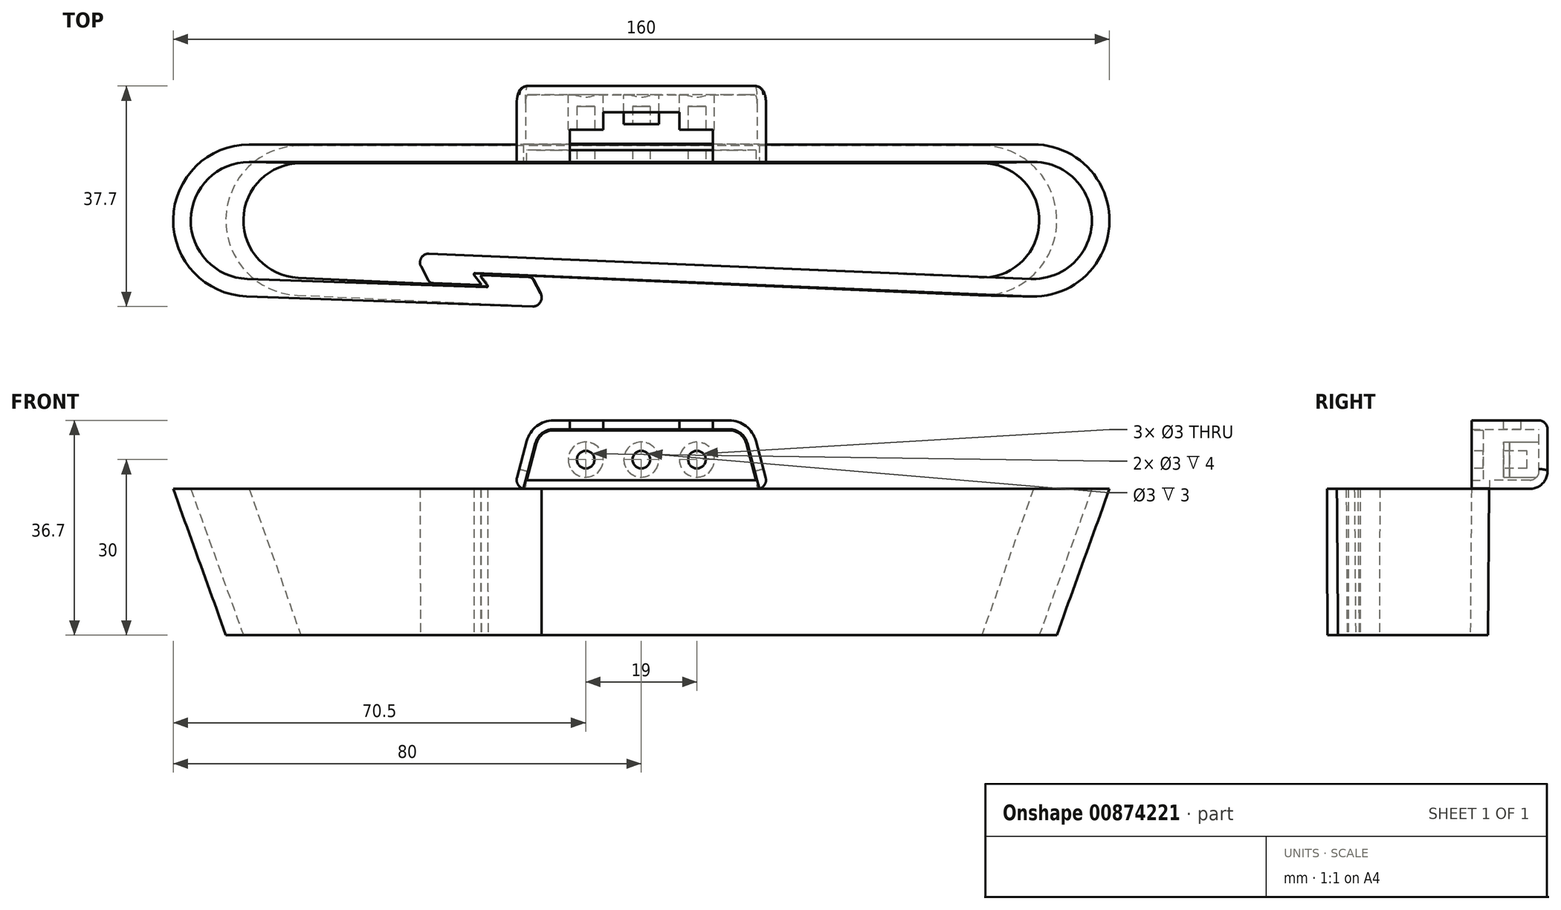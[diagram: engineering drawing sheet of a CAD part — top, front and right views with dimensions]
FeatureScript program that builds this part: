
annotation { "Feature Type Name" : "Feature", "Feature Type Description" : "" }
export const myFeature = defineFeature(function(context is Context, id is Id, definition is map)
    precondition{}
    {
        {
            var Q0;
            Q0=qCreatedBy(makeId("Top.planeOp"),FACE);
            var sketch = newSketch(context, id + "F0", { "sketchPlane" : qUnion([Q0])});
            skPoint(sketch, "E0.middle", {"position": v(0, 0) * mm});
            skArc(sketch, "E1", {"start": v(66.46, -12.99) * mm, "mid": v(80, -0.27) * mm, "end": v(67, 13) * mm});
            skLineSegment(sketch, "E2", {"start": v(67, 13) * mm, "end": v(-67, 13) * mm});
            skArc(sketch, "E3", {"start": v(-67, 13) * mm, "mid": v(-80, 0.23) * mm, "end": v(-67.45, -13) * mm});
            skLineSegment(sketch, "E4", {"start": v(66.46, -12.99) * mm, "end": v(-28.42, -9.01) * mm});
            skLineSegment(sketch, "E5", {"start": v(0, 13) * mm, "end": v(0, -10.2) * mm, "construction": true});
            skLineSegment(sketch, "E6", {"start": v(-16, 0) * mm, "end": v(-16, -14.79) * mm, "construction": true});
            skLineSegment(sketch, "E7", {"start": v(-67.45, -13) * mm, "end": v(-18.6, -14.7) * mm});
            skLineSegment(sketch, "E8", {"start": v(-67, 0) * mm, "end": v(-16, 0) * mm, "construction": true});
            skLineSegment(sketch, "E9.0", {"start": v(66.58, -10) * mm, "end": v(-36.26, -5.68) * mm});
            skLineSegment(sketch, "E9.1", {"start": v(-67.35, -10) * mm, "end": v(-26.46, -11.42) * mm});
            skArc(sketch, "E9.2", {"start": v(-67, 10) * mm, "mid": v(-77, 0.17) * mm, "end": v(-67.35, -10) * mm});
            skLineSegment(sketch, "E9.3", {"start": v(67, 10) * mm, "end": v(-67, 10) * mm});
            skArc(sketch, "E9.4", {"start": v(66.58, -10) * mm, "mid": v(77, -0.2) * mm, "end": v(67, 10) * mm});
            skLineSegment(sketch, "E10", {"start": v(-27.2, -9.4) * mm, "end": v(-19.29, -9.67) * mm});
            skLineSegment(sketch, "E11", {"start": v(-18.44, -10.2) * mm, "end": v(-17.22, -12.5) * mm});
            skPoint(sketch, "E12.visualSharp", {"position": v(-16, -14.79) * mm});
            skArc(sketch, "E12.filletArc", {"start": v(-18.6, -14.7) * mm, "mid": v(-17.27, -14) * mm, "end": v(-17.22, -12.5) * mm});
            skPoint(sketch, "E13.visualSharp", {"position": v(-18.71, -9.7) * mm});
            skArc(sketch, "E13.filletArc", {"start": v(-18.44, -10.2) * mm, "mid": v(-18.8, -9.82) * mm, "end": v(-19.29, -9.67) * mm});
            skPoint(sketch, "E14.visualSharp", {"position": v(-27.2, -9.4) * mm});
            skArc(sketch, "E14.filletArc", {"start": v(-27.2, -9.4) * mm, "mid": v(-27.4, -9.5) * mm, "end": v(-27.37, -9.72) * mm});
            skLineSegment(sketch, "E15", {"start": v(0, 0) * mm, "end": v(67, 0) * mm, "construction": true});
            skLineSegment(sketch, "E16", {"start": v(-28.59, -9.33) * mm, "end": v(-27.52, -10.72) * mm});
            skLineSegment(sketch, "E17", {"start": v(-27.69, -11.04) * mm, "end": v(-35.6, -10.71) * mm});
            skLineSegment(sketch, "E18", {"start": v(-36.45, -10.18) * mm, "end": v(-37.65, -7.87) * mm});
            skPoint(sketch, "E19.visualSharp", {"position": v(-36.18, -10.69) * mm});
            skArc(sketch, "E19.filletArc", {"start": v(-36.45, -10.18) * mm, "mid": v(-36.1, -10.56) * mm, "end": v(-35.6, -10.71) * mm});
            skPoint(sketch, "E20.visualSharp", {"position": v(-38.85, -5.57) * mm});
            skArc(sketch, "E20.filletArc", {"start": v(-36.26, -5.68) * mm, "mid": v(-37.59, -6.38) * mm, "end": v(-37.65, -7.87) * mm});
            skArc(sketch, "E21.filletArc", {"start": v(-27.69, -11.04) * mm, "mid": v(-27.5, -10.94) * mm, "end": v(-27.52, -10.72) * mm});
            skPoint(sketch, "E22.visualSharp", {"position": v(-28.85, -9) * mm});
            skArc(sketch, "E22.filletArc", {"start": v(-28.42, -9.01) * mm, "mid": v(-28.6, -9.12) * mm, "end": v(-28.59, -9.33) * mm});
            skLineSegment(sketch, "E23", {"start": v(-16, 0) * mm, "end": v(0, 0) * mm, "construction": true});
            skArc(sketch, "E24", {"start": v(-26.46, -11.42) * mm, "mid": v(-26.27, -11.31) * mm, "end": v(-26.3, -11.1) * mm});
            skLineSegment(sketch, "E25", {"start": v(-27.37, -9.72) * mm, "end": v(-26.3, -11.1) * mm});
            skLineSegment(sketch, "E26", {"start": v(-27.37, -9.47) * mm, "end": v(-27.37, -10.97) * mm, "construction": true});
            skLineSegment(sketch, "E27", {"start": v(-27.52, -10.72) * mm, "end": v(-27.52, -9.22) * mm, "construction": true});
            skSolve(sketch);
        }
        {
            var Q0;
            Q0=qCreatedBy(makeId("Top.planeOp"),FACE);
            cPlane(context, id + "F1", {"entities" : qUnion([Q0]), "cplaneType" : CPlaneType.OFFSET, "offset" : 25 * mm, "oppositeDirection" : true, "width" : 150 * mm, "height" : 150 * mm});
        }
        {
            var Q0;
            Q0=qCreatedBy(id+"F1.planeOp",FACE);
            var sketch = newSketch(context, id + "F2", { "sketchPlane" : qUnion([Q0])});
            skPoint(sketch, "E28.middle", {"position": v(0, 0) * mm});
            skArc(sketch, "E29", {"start": v(57.64, -12.79) * mm, "mid": v(71, -0.28) * mm, "end": v(58.2, 12.8) * mm});
            skLineSegment(sketch, "E30", {"start": v(58.2, 12.8) * mm, "end": v(-58.2, 12.8) * mm});
            skArc(sketch, "E31", {"start": v(-58.2, 12.8) * mm, "mid": v(-71, 0.3) * mm, "end": v(-58.78, -12.79) * mm});
            skLineSegment(sketch, "E32", {"start": v(57.64, -12.79) * mm, "end": v(-28.37, -9.03) * mm});
            skLineSegment(sketch, "E33", {"start": v(0, 12.8) * mm, "end": v(0, -10.27) * mm, "construction": true});
            skLineSegment(sketch, "E34", {"start": v(-16, 0) * mm, "end": v(-16, -14.73) * mm, "construction": true});
            skLineSegment(sketch, "E35", {"start": v(-58.78, -12.79) * mm, "end": v(-18.6, -14.61) * mm});
            skLineSegment(sketch, "E36", {"start": v(-58.2, 0) * mm, "end": v(-16, 0) * mm, "construction": true});
            skLineSegment(sketch, "E37.0", {"start": v(57.77, -9.8) * mm, "end": v(-36.2, -5.69) * mm});
            skLineSegment(sketch, "E37.1", {"start": v(-58.64, -9.79) * mm, "end": v(-26.42, -11.25) * mm});
            skArc(sketch, "E37.2", {"start": v(-58.2, 9.8) * mm, "mid": v(-68, 0.22) * mm, "end": v(-58.64, -9.79) * mm});
            skLineSegment(sketch, "E37.3", {"start": v(58.2, 9.8) * mm, "end": v(-58.2, 9.8) * mm});
            skArc(sketch, "E37.4", {"start": v(57.77, -9.8) * mm, "mid": v(68, -0.21) * mm, "end": v(58.2, 9.8) * mm});
            skLineSegment(sketch, "E38", {"start": v(-27.15, -9.22) * mm, "end": v(-19.23, -9.58) * mm});
            skLineSegment(sketch, "E39", {"start": v(-18.4, -10.12) * mm, "end": v(-17.2, -12.42) * mm});
            skPoint(sketch, "E40.visualSharp", {"position": v(-16, -14.73) * mm});
            skArc(sketch, "E40.filletArc", {"start": v(-18.6, -14.61) * mm, "mid": v(-17.26, -13.92) * mm, "end": v(-17.2, -12.42) * mm});
            skPoint(sketch, "E41.visualSharp", {"position": v(-18.66, -9.6) * mm});
            skArc(sketch, "E41.filletArc", {"start": v(-18.4, -10.12) * mm, "mid": v(-18.74, -9.73) * mm, "end": v(-19.23, -9.58) * mm});
            skPoint(sketch, "E42.visualSharp", {"position": v(-27.15, -9.22) * mm});
            skArc(sketch, "E42.filletArc", {"start": v(-27.15, -9.22) * mm, "mid": v(-27.33, -9.33) * mm, "end": v(-27.32, -9.54) * mm});
            skLineSegment(sketch, "E43", {"start": v(0, 0) * mm, "end": v(58.2, 0) * mm, "construction": true});
            skLineSegment(sketch, "E44", {"start": v(-28.53, -9.35) * mm, "end": v(-27.47, -10.74) * mm});
            skLineSegment(sketch, "E45", {"start": v(-27.63, -11.07) * mm, "end": v(-35.55, -10.72) * mm});
            skLineSegment(sketch, "E46", {"start": v(-36.4, -10.18) * mm, "end": v(-37.6, -7.88) * mm});
            skPoint(sketch, "E47.visualSharp", {"position": v(-36.13, -10.7) * mm});
            skArc(sketch, "E47.filletArc", {"start": v(-36.4, -10.18) * mm, "mid": v(-36.04, -10.57) * mm, "end": v(-35.55, -10.72) * mm});
            skPoint(sketch, "E48.visualSharp", {"position": v(-38.8, -5.57) * mm});
            skArc(sketch, "E48.filletArc", {"start": v(-36.2, -5.69) * mm, "mid": v(-37.53, -6.38) * mm, "end": v(-37.6, -7.88) * mm});
            skArc(sketch, "E49.filletArc", {"start": v(-27.63, -11.07) * mm, "mid": v(-27.45, -10.96) * mm, "end": v(-27.47, -10.74) * mm});
            skPoint(sketch, "E50.visualSharp", {"position": v(-28.8, -9.01) * mm});
            skArc(sketch, "E50.filletArc", {"start": v(-28.37, -9.03) * mm, "mid": v(-28.55, -9.14) * mm, "end": v(-28.53, -9.35) * mm});
            skLineSegment(sketch, "E51", {"start": v(-16, 0) * mm, "end": v(0, 0) * mm, "construction": true});
            skArc(sketch, "E52", {"start": v(-26.42, -11.25) * mm, "mid": v(-26.23, -11.15) * mm, "end": v(-26.25, -10.93) * mm});
            skLineSegment(sketch, "E53", {"start": v(-27.32, -9.54) * mm, "end": v(-26.25, -10.93) * mm});
            skLineSegment(sketch, "E54", {"start": v(-27.32, -9.3) * mm, "end": v(-27.32, -10.8) * mm, "construction": true});
            skLineSegment(sketch, "E55", {"start": v(-27.47, -10.74) * mm, "end": v(-27.47, -9.24) * mm, "construction": true});
            skSolve(sketch);
        }
        {
            var Q0;
            Q0=qSketchRegion(id+"F0",true);
            var Q1;
            Q1=qSketchRegion(id+"F2",true);
            loft(context, id + "F3", {"sheetProfilesArray" : [{ "sheetProfileEntities" : qUnion([Q0]) }, { "sheetProfileEntities" : qUnion([Q1]) }]});
        }
        {
            var Q0;
            Q0=qCreatedBy(makeId("Top.planeOp"),FACE);
            var sketch = newSketch(context, id + "F4", { "sketchPlane" : qUnion([Q0])});
            skLineSegment(sketch, "E56", {"start": v(20, 12) * mm, "end": v(20, 10) * mm});
            skLineSegment(sketch, "E57", {"start": v(20, 10) * mm, "end": v(-20, 10) * mm});
            skLineSegment(sketch, "E58", {"start": v(-20, 10) * mm, "end": v(-20, 12) * mm});
            skLineSegment(sketch, "E59", {"start": v(-20, 12) * mm, "end": v(20, 12) * mm});
            skPoint(sketch, "E60.visualSharp", {"position": v(-20, 10) * mm});
            skPoint(sketch, "E61.visualSharp", {"position": v(20, 10) * mm});
            skLineSegment(sketch, "E62", {"start": v(0, 10) * mm, "end": v(0, 12) * mm, "construction": true});
            skPoint(sketch, "E62.endSnap0", {"position": v(0, 12) * mm});
            skSolve(sketch);
        }
        {
            var Q0;
            Q0=qSketchRegion(id+"F4",true);
            extrude(context, id + "F5", {"entities" : qUnion([Q0]), "operationType" : NewBodyOperationType.ADD, "depth" : 10 * mm, "offsetDistance" : 25 * mm});
        }
        {
            var Q0;
            Q0=makeQuery(id+"F5.opExtrude","SWEPT_FACE",FACE,{"disambiguationData":[OSD([sQuery(id+"F4.wireOp",EDGE,"E57")])]});
            var sketch = newSketch(context, id + "F6", { "sketchPlane" : qUnion([Q0])});
            skLineSegment(sketch, "E63", {"start": v(0, 10) * mm, "end": v(0, 5) * mm, "construction": true});
            skCircle(sketch, "E64", {"center": v(0, 5) * mm, "radius": 1.5 * mm});
            skCircle(sketch, "E65", {"center": v(9.5, 5) * mm, "radius": 1.5 * mm});
            skCircle(sketch, "E66", {"center": v(-9.5, 5) * mm, "radius": 1.5 * mm});
            skSolve(sketch);
        }
        {
            var Q0;
            Q0=qSketchRegion(id+"F6",true);
            extrude(context, id + "F7", {"entities" : qUnion([Q0]), "operationType" : NewBodyOperationType.REMOVE, "endBound" : BoundingType.THROUGH_ALL, "oppositeDirection" : true, "depth" : 25 * mm, "offsetDistance" : 25 * mm});
        }
        {
            var Q0;
            Q0=makeQuery(id+"F5.opExtrude","CAP_EDGE",EDGE,{"disambiguationData":[OSD([sQuery(id+"F4.wireOp",EDGE,"E58")])],"isStart":false});
            var Q1;
            Q1=makeQuery(id+"F5.opExtrude","CAP_EDGE",EDGE,{"disambiguationData":[OSD([sQuery(id+"F4.wireOp",EDGE,"E56")])],"isStart":false});
            chamfer(context, id + "F8", {"entities" : qUnion([Q0, Q1]), "chamferType" : ChamferType.OFFSET_ANGLE, "width" : 10 * mm, "oppositeDirection" : false, "angle" : 15 * degree, "tangentPropagation" : true});
        }
        {
            var Q0;
            {var subQ0=sQuery(id+"F4.wireOp",EDGE,"E58");Q0=makeQuery(id+"F8.opChamfer","BLEND_EDGE",EDGE,{"blendedFrom":[makeQuery(id+"F5.opExtrude","CAP_EDGE",EDGE,{"disambiguationData":[OSD([subQ0])],"isStart":false}),makeQuery(id+"F5.opExtrude","CAP_FACE",FACE,{"disambiguationData":[OSD([sQuery(id+"F4.wireOp",EDGE,"E56"),sQuery(id+"F4.wireOp",EDGE,"E57"),subQ0,sQuery(id+"F4.wireOp",EDGE,"E59")])],"isStart":false})],"blendedInto":[makeQuery(id+"F5.opExtrude","CAP_FACE",FACE,{"disambiguationData":[OSD([sQuery(id+"F4.wireOp",EDGE,"E56"),sQuery(id+"F4.wireOp",EDGE,"E57"),subQ0,sQuery(id+"F4.wireOp",EDGE,"E59")])],"isStart":false})]});}
            var Q1;
            {var subQ0=sQuery(id+"F4.wireOp",EDGE,"E56");Q1=makeQuery(id+"F8.opChamfer","BLEND_EDGE",EDGE,{"blendedFrom":[makeQuery(id+"F5.opExtrude","CAP_EDGE",EDGE,{"disambiguationData":[OSD([subQ0])],"isStart":false}),makeQuery(id+"F5.opExtrude","CAP_FACE",FACE,{"disambiguationData":[OSD([subQ0,sQuery(id+"F4.wireOp",EDGE,"E57"),sQuery(id+"F4.wireOp",EDGE,"E58"),sQuery(id+"F4.wireOp",EDGE,"E59")])],"isStart":false})],"blendedInto":[makeQuery(id+"F5.opExtrude","CAP_FACE",FACE,{"disambiguationData":[OSD([subQ0,sQuery(id+"F4.wireOp",EDGE,"E57"),sQuery(id+"F4.wireOp",EDGE,"E58"),sQuery(id+"F4.wireOp",EDGE,"E59")])],"isStart":false})]});}
            fillet(context, id + "F9", {"entities" : qUnion([Q0, Q1]), "radius" : 3 * mm, "tangentPropagation" : true, "allowEdgeOverflow" : false});
        }
        {
            var Q0;
            Q0=makeQuery(id+"F5.opExtrude","SWEPT_FACE",FACE,{"disambiguationData":[OSD([sQuery(id+"F4.wireOp",EDGE,"E57")])]});
            cPlane(context, id + "F10", {"entities" : qUnion([Q0]), "cplaneType" : CPlaneType.OFFSET, "offset" : 0 * mm, "oppositeDirection" : true, "width" : 150 * mm, "height" : 150 * mm});
        }
        {
            var Q0;
            Q0=qCreatedBy(id+"F10.planeOp",FACE);
            var sketch = newSketch(context, id + "F11", { "sketchPlane" : qUnion([Q0])});
            skLineSegment(sketch, "E67.0", {"start": v(-19.56, 8.22) * mm, "end": v(-21.76, 0) * mm});
            skLineSegment(sketch, "E67.1", {"start": v(21.76, 0) * mm, "end": v(19.56, 8.22) * mm});
            skArc(sketch, "E67.2", {"start": v(19.56, 8.22) * mm, "mid": v(17.88, 10.73) * mm, "end": v(15.02, 11.7) * mm});
            skLineSegment(sketch, "E67.3", {"start": v(15.02, 11.7) * mm, "end": v(-15.02, 11.7) * mm});
            skArc(sketch, "E67.4", {"start": v(-15.02, 11.7) * mm, "mid": v(-17.88, 10.73) * mm, "end": v(-19.56, 8.22) * mm});
            skLineSegment(sketch, "E68", {"start": v(-21.76, 0) * mm, "end": v(21.76, 0) * mm});
            skSolve(sketch);
        }
        {
            var Q0;
            Q0 = qSketchRegion(id + "F11", true);
            extrude(context, id + "F12", {"entities" : qUnion([Q0]), "oppositeDirection" : true, "depth" : 13 * mm, "offsetDistance" : 25 * mm});
        }
        {
            var Q0;
            Q0=makeQuery(id+"F12.opExtrude","CAP_EDGE",EDGE,{"disambiguationData":[OSD([sQuery(id+"F11.wireOp",EDGE,"E68")])],"isStart":false});
            fillet(context, id + "F13", {"entities" : qUnion([Q0]), "radius" : 3 * mm, "tangentPropagation" : true, "allowEdgeOverflow" : false});
        }
        {
            var Q0;
            Q0=makeQuery(id+"F12.opExtrude","CAP_FACE",FACE,{"disambiguationData":[OSD([sQuery(id+"F11.wireOp",EDGE,"E67.0"),sQuery(id+"F11.wireOp",EDGE,"E67.1"),sQuery(id+"F11.wireOp",EDGE,"E67.2"),sQuery(id+"F11.wireOp",EDGE,"E67.3"),sQuery(id+"F11.wireOp",EDGE,"E67.4"),sQuery(id+"F11.wireOp",EDGE,"E68")])],"isStart":true});
            shell(context, id + "F14", {"entities" : qUnion([Q0]), "thickness" : 1.5 * mm});
        }
        {
            var Q0;
            Q0=makeQuery(id+"F12.opExtrude","CAP_FACE",FACE,{"disambiguationData":[OSD([sQuery(id+"F11.wireOp",EDGE,"E67.0"),sQuery(id+"F11.wireOp",EDGE,"E67.1"),sQuery(id+"F11.wireOp",EDGE,"E67.2"),sQuery(id+"F11.wireOp",EDGE,"E67.3"),sQuery(id+"F11.wireOp",EDGE,"E67.4"),sQuery(id+"F11.wireOp",EDGE,"E68")])],"isStart":true});
            var sketch = newSketch(context, id + "F15", { "sketchPlane" : qUnion([Q0])});
            skLineSegment(sketch, "E69", {"start": v(-19.8, 1.5) * mm, "end": v(19.8, 1.5) * mm});
            skLineSegment(sketch, "E70", {"start": v(19.8, 1.5) * mm, "end": v(20.2, 0) * mm});
            skLineSegment(sketch, "E71", {"start": v(20.2, 0) * mm, "end": v(-20.2, 0) * mm});
            skLineSegment(sketch, "E72", {"start": v(-20.2, 0) * mm, "end": v(-19.8, 1.5) * mm});
            skPoint(sketch, "E73", {"position": v(0, 0) * mm});
            skSolve(sketch);
        }
        {
            var Q0;
            Q0 = qSketchRegion(id + "F15", true);
            extrude(context, id + "F16", {"entities" : qUnion([Q0]), "operationType" : NewBodyOperationType.REMOVE, "oppositeDirection" : true, "depth" : 3.1 * mm, "offsetDistance" : 25 * mm});
        }
        {
            var Q0;
            Q0=makeQuery(id+"F12.opExtrude","SWEPT_EDGE",EDGE,{"disambiguationData":[OSD([sQuery(id+"F11.wireOp",EDGE,"E67.1"),sQuery(id+"F11.wireOp",EDGE,"E68")])]});
            fillet(context, id + "F17", {"entities" : qUnion([Q0]), "radius" : 1.5 * mm, "tangentPropagation" : true, "allowEdgeOverflow" : false});
        }
        {
            var Q0;
            Q0=makeQuery(id+"F14.opShell","OFFSET_FACE",FACE,{"disambiguationData":[OSD([sQuery(id+"F11.wireOp",EDGE,"E67.0"),sQuery(id+"F11.wireOp",EDGE,"E67.1"),sQuery(id+"F11.wireOp",EDGE,"E67.2"),sQuery(id+"F11.wireOp",EDGE,"E67.3"),sQuery(id+"F11.wireOp",EDGE,"E67.4"),sQuery(id+"F11.wireOp",EDGE,"E68")])]});
            var sketch = newSketch(context, id + "F18", { "sketchPlane" : qUnion([Q0])});
            skCircle(sketch, "E74", {"center": v(0, 5) * mm, "radius": 3 * mm});
            skCircle(sketch, "E75", {"center": v(9.5, 5) * mm, "radius": 3 * mm});
            skCircle(sketch, "E76", {"center": v(-9.5, 5) * mm, "radius": 3 * mm});
            skSolve(sketch);
        }
        {
            var Q0;
            Q0=makeQuery(id+"F18.imprint","IMPRINT",FACE,{"disambiguationData":[TD([[makeQuery(id+"F18.imprint","IMPRINT",EDGE,{"derivedFrom":sQuery(id+"F18.wireOp",EDGE,"E76")}),1.0]])]});
            var Q1;
            Q1=makeQuery(id+"F18.imprint","IMPRINT",FACE,{"disambiguationData":[TD([[makeQuery(id+"F18.imprint","IMPRINT",EDGE,{"derivedFrom":sQuery(id+"F18.wireOp",EDGE,"E75")}),1.0]])]});
            extrude(context, id + "F19", {"entities" : qUnion([Q0, Q1]), "operationType" : NewBodyOperationType.ADD, "depth" : 6 * mm, "offsetDistance" : 25 * mm});
        }
        {
            var Q0;
            Q0=makeQuery(id+"F18.imprint","IMPRINT",FACE,{"disambiguationData":[TD([[makeQuery(id+"F18.imprint","IMPRINT",EDGE,{"derivedFrom":sQuery(id+"F18.wireOp",EDGE,"E74")}),1.0]])]});
            extrude(context, id + "F20", {"entities" : qUnion([Q0]), "operationType" : NewBodyOperationType.ADD, "depth" : 5 * mm, "offsetDistance" : 25 * mm});
        }
        {
            var Q0;
            Q0=makeQuery(id+"F6.imprint","IMPRINT",FACE,{"disambiguationData":[TD([[makeQuery(id+"F6.imprint","IMPRINT",EDGE,{"derivedFrom":sQuery(id+"F6.wireOp",EDGE,"E66")}),1.0]])]});
            var Q1;
            Q1=makeQuery(id+"F6.imprint","IMPRINT",FACE,{"disambiguationData":[TD([[makeQuery(id+"F6.imprint","IMPRINT",EDGE,{"derivedFrom":sQuery(id+"F6.wireOp",EDGE,"E64")}),1.0]])]});
            var Q2;
            Q2=makeQuery(id+"F6.imprint","IMPRINT",FACE,{"disambiguationData":[TD([[makeQuery(id+"F6.imprint","IMPRINT",EDGE,{"derivedFrom":sQuery(id+"F6.wireOp",EDGE,"E65")}),1.0]])]});
            extrude(context, id + "F21", {"entities" : qUnion([Q0, Q1, Q2]), "operationType" : NewBodyOperationType.REMOVE, "oppositeDirection" : true, "depth" : (11 - 1.5) * mm, "offsetDistance" : 25 * mm});
        }
        {
            var Q0;
            Q0=makeQuery(id+"F12.opExtrude","SWEPT_FACE",FACE,{"disambiguationData":[OSD([sQuery(id+"F11.wireOp",EDGE,"E67.3")])]});
            var sketch = newSketch(context, id + "F22", { "sketchPlane" : qUnion([Q0])});
            skLineSegment(sketch, "E77", {"start": v(-12.25, 10) * mm, "end": v(-12.25, 15.5) * mm});
            skLineSegment(sketch, "E78", {"start": v(-12.25, 15.5) * mm, "end": v(-6.5, 15.5) * mm});
            skLineSegment(sketch, "E79", {"start": v(-6.5, 15.5) * mm, "end": v(-6.5, 18.5) * mm});
            skLineSegment(sketch, "E80", {"start": v(-6.5, 18.5) * mm, "end": v(6.5, 18.5) * mm});
            skLineSegment(sketch, "E81", {"start": v(6.5, 18.5) * mm, "end": v(6.5, 15.5) * mm});
            skLineSegment(sketch, "E82", {"start": v(6.5, 15.5) * mm, "end": v(12.25, 15.5) * mm});
            skLineSegment(sketch, "E83", {"start": v(12.25, 15.5) * mm, "end": v(12.25, 10) * mm});
            skLineSegment(sketch, "E84", {"start": v(12.25, 10) * mm, "end": v(-12.25, 10) * mm});
            skPoint(sketch, "E85", {"position": v(0, 10) * mm});
            skSolve(sketch);
        }
        {
            var Q0;
            Q0 = qSketchRegion(id + "F22", true);
            extrude(context, id + "F23", {"entities" : qUnion([Q0]), "operationType" : NewBodyOperationType.REMOVE, "oppositeDirection" : true, "depth" : 1.5 * mm, "offsetDistance" : 25 * mm});
        }
    });
